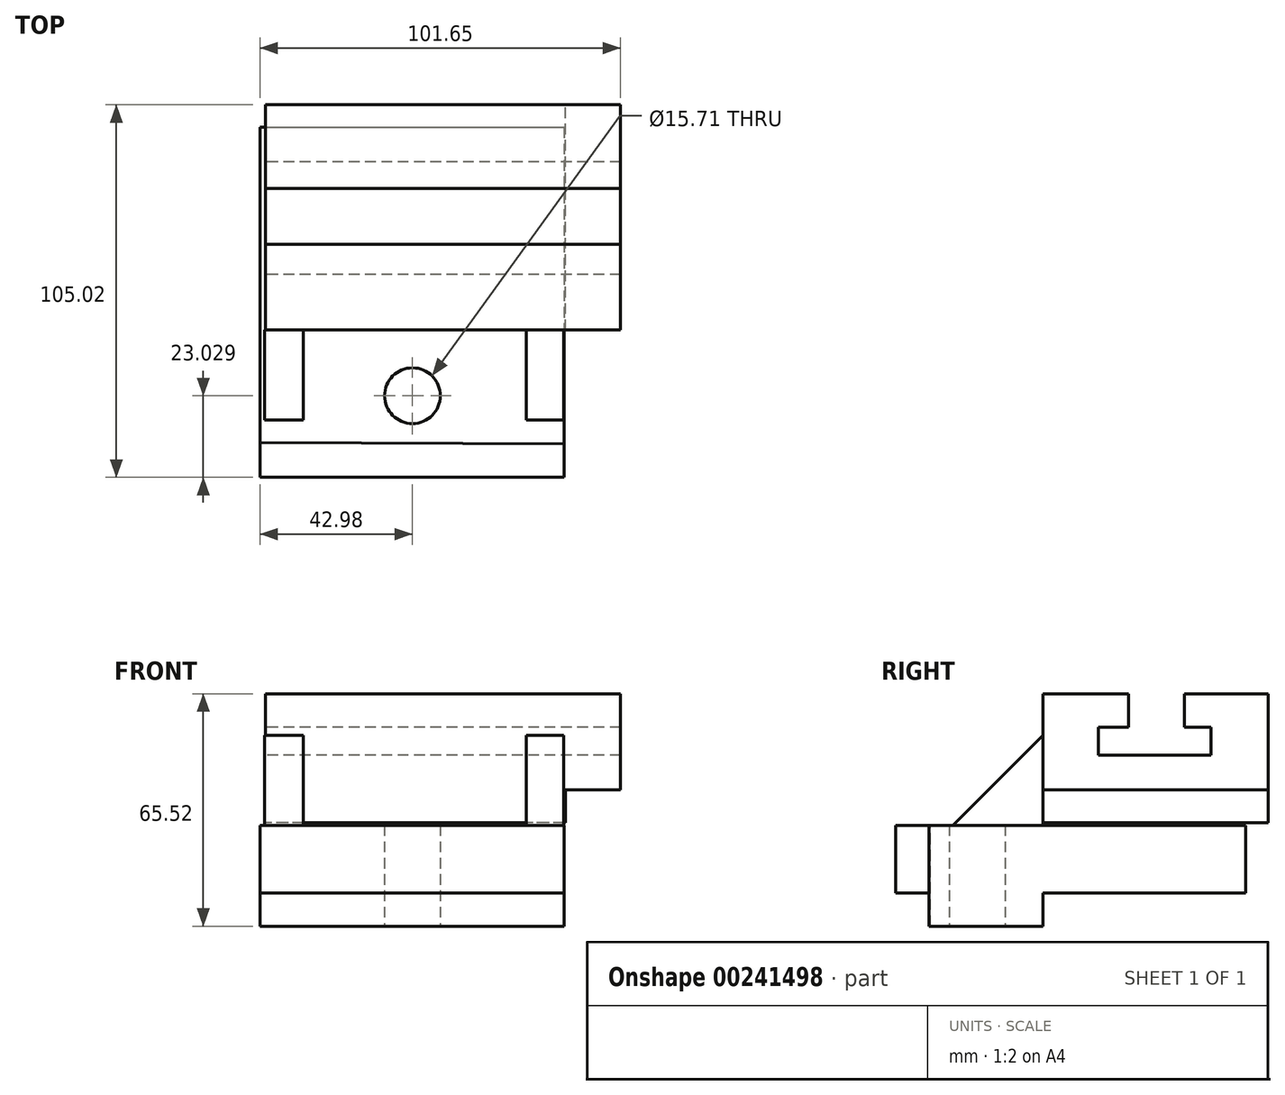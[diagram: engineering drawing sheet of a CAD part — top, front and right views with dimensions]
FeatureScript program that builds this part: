
annotation { "Feature Type Name" : "Feature", "Feature Type Description" : "" }
export const myFeature = defineFeature(function(context is Context, id is Id, definition is map)
    precondition{}
    {
        {
            var Q0;
            Q0=qCreatedBy(makeId("Top.planeOp"),FACE);
            var sketch = newSketch(context, id + "F0", { "sketchPlane" : qUnion([Q0])});
            skLineSegment(sketch, "E0", {"start": v(-42.94, 57.15) * mm, "end": v(42.75, 57.15) * mm});
            skLineSegment(sketch, "E1", {"start": v(42.75, 57.15) * mm, "end": v(42.75, -32.12) * mm});
            skLineSegment(sketch, "E2", {"start": v(42.38, -31.75) * mm, "end": v(-42.94, -31.75) * mm});
            skLineSegment(sketch, "E3", {"start": v(-42.94, -31.75) * mm, "end": v(-42.94, 57.15) * mm});
            skLineSegment(sketch, "E4", {"start": v(-42.94, 0) * mm, "end": v(42.75, 0) * mm});
            skLineSegment(sketch, "E5", {"start": v(-42.94, -31.75) * mm, "end": v(42.75, -32.12) * mm});
            skLineSegment(sketch, "E6", {"start": v(-42.94, -31.75) * mm, "end": v(-42.98, -41.52) * mm});
            skLineSegment(sketch, "E7", {"start": v(-42.98, -41.52) * mm, "end": v(42.75, -41.52) * mm});
            skLineSegment(sketch, "E8", {"start": v(42.75, -41.52) * mm, "end": v(42.75, -32.12) * mm});
            skSolve(sketch);
        }
        {
            var Q0;
            {var subQ0=sQuery(id+"F0.wireOp",EDGE,"E0");Q0=makeQuery(id+"F0.imprint","IMPRINT",FACE,{"disambiguationData":[TD([[makeQuery(id+"F0.imprint","IMPRINT",EDGE,{"derivedFrom":subQ0}),-1.0]])]});}
            extrude(context, id + "F1", {"entities" : qUnion([Q0]), "oppositeDirection" : true, "depth" : 19.05 * mm});
        }
        {
            var Q0;
            {var subQ2=sQuery(id+"F0.wireOp",EDGE,"E6");Q0=makeQuery(id+"F0.imprint","IMPRINT",FACE,{"disambiguationData":[TD([[makeQuery(id+"F0.imprint","IMPRINT",EDGE,{"derivedFrom":subQ2}),1.0]])]});}
            extrude(context, id + "F2", {"entities" : qUnion([Q0]), "oppositeDirection" : true, "depth" : 19.05 * mm});
        }
        {
            var Q0;
            {var subQ2=sQuery(id+"F0.wireOp",EDGE,"E4");Q0=makeQuery(id+"F0.imprint","IMPRINT",FACE,{"disambiguationData":[TD([[makeQuery(id+"F0.imprint","IMPRINT",EDGE,{"derivedFrom":subQ2}),-1.0]])]});}
            extrude(context, id + "F3", {"entities" : qUnion([Q0]), "oppositeDirection" : true, "depth" : 28.45 * mm});
        }
        {
            var Q0;
            Q0=qCreatedBy(makeId("Right.planeOp"),FACE);
            var sketch = newSketch(context, id + "F4", { "sketchPlane" : qUnion([Q0])});
            skLineSegment(sketch, "E9", {"start": v(0, 0) * mm, "end": v(-25.4, 0) * mm});
            skLineSegment(sketch, "E10", {"start": v(-25.4, 0) * mm, "end": v(0, 25.4) * mm});
            skLineSegment(sketch, "E11", {"start": v(0, 25.4) * mm, "end": v(0, 0) * mm});
            skSolve(sketch);
        }
        {
            var Q0;
            Q0=makeQuery(id+"F4.imprint","IMPRINT",FACE,{"disambiguationData":[TD([[makeQuery(id+"F4.imprint","IMPRINT",EDGE,{"derivedFrom":sQuery(id+"F4.wireOp",EDGE,"E9")}),-1.0]])]});
            extrude(context, id + "F5", {"entities" : qUnion([Q0]), "operationType" : NewBodyOperationType.ADD, "depth" : 42.67 * mm, "hasSecondDirection" : true, "secondDirectionOppositeDirection" : true, "secondDirectionDepth" : 41.66 * mm});
        }
        {
            var Q0;
            Q0=qCreatedBy(makeId("Front.planeOp"),FACE);
            var sketch = newSketch(context, id + "F6", { "sketchPlane" : qUnion([Q0])});
            skLineSegment(sketch, "E12", {"start": v(-30.76, 27) * mm, "end": v(-30.76, 0) * mm});
            skLineSegment(sketch, "E13", {"start": v(-30.76, 27) * mm, "end": v(32.07, 27) * mm});
            skLineSegment(sketch, "E14", {"start": v(32.07, 27) * mm, "end": v(32.07, 0) * mm});
            skLineSegment(sketch, "E15", {"start": v(32.07, 0) * mm, "end": v(-30.76, 0) * mm});
            skSolve(sketch);
        }
        {
            var Q0;
            Q0 = qSketchRegion(id + "F6", true);
            extrude(context, id + "F7", {"entities" : qUnion([Q0]), "operationType" : NewBodyOperationType.REMOVE, "depth" : 187.45 * mm});
        }
        {
            var Q0;
            Q0=qCreatedBy(makeId("Right.planeOp"),FACE);
            var sketch = newSketch(context, id + "F8", { "sketchPlane" : qUnion([Q0])});
            skLineSegment(sketch, "E16", {"start": v(0, 0.75) * mm, "end": v(63.5, 0.75) * mm});
            skLineSegment(sketch, "E17", {"start": v(0, 0.75) * mm, "end": v(0, 37.07) * mm});
            skLineSegment(sketch, "E18", {"start": v(0, 37.07) * mm, "end": v(24.14, 37.07) * mm});
            skLineSegment(sketch, "E19", {"start": v(63.5, 0.75) * mm, "end": v(63.5, 37.07) * mm});
            skLineSegment(sketch, "E20", {"start": v(63.5, 37.07) * mm, "end": v(39.89, 37.07) * mm});
            skLineSegment(sketch, "E21", {"start": v(39.89, 37.07) * mm, "end": v(39.89, 27.67) * mm});
            skLineSegment(sketch, "E22", {"start": v(39.89, 27.67) * mm, "end": v(47.45, 27.67) * mm});
            skLineSegment(sketch, "E23", {"start": v(24.14, 37.07) * mm, "end": v(24.14, 27.67) * mm});
            skLineSegment(sketch, "E24", {"start": v(24.22, 27.67) * mm, "end": v(15.7, 27.67) * mm});
            skLineSegment(sketch, "E25", {"start": v(15.7, 27.67) * mm, "end": v(15.7, 19.8) * mm});
            skLineSegment(sketch, "E26", {"start": v(15.7, 19.8) * mm, "end": v(47.46, 19.8) * mm});
            skLineSegment(sketch, "E27", {"start": v(47.46, 19.8) * mm, "end": v(47.45, 27.67) * mm});
            skSolve(sketch);
        }
        {
            var Q0;
            Q0 = qSketchRegion(id + "F8", true);
            extrude(context, id + "F9", {"entities" : qUnion([Q0]), "depth" : 58.67 * mm, "hasSecondDirection" : true, "secondDirectionOppositeDirection" : true, "secondDirectionDepth" : 41.4 * mm});
        }
        {
            var Q0;
            Q0=qCreatedBy(makeId("Front.planeOp"),FACE);
            var sketch = newSketch(context, id + "F10", { "sketchPlane" : qUnion([Q0])});
            skLineSegment(sketch, "E28", {"start": v(43.2, 9.98) * mm, "end": v(60.21, 9.98) * mm});
            skLineSegment(sketch, "E29", {"start": v(60.21, 9.98) * mm, "end": v(60.21, 0) * mm});
            skLineSegment(sketch, "E30", {"start": v(60.21, 0) * mm, "end": v(43.2, 0) * mm});
            skLineSegment(sketch, "E31", {"start": v(43.2, 0) * mm, "end": v(43.2, 9.98) * mm});
            skSolve(sketch);
        }
        {
            var Q0;
            Q0 = qSketchRegion(id + "F10", true);
            extrude(context, id + "F11", {"entities" : qUnion([Q0]), "operationType" : NewBodyOperationType.REMOVE, "oppositeDirection" : true, "depth" : 129.29 * mm});
        }
        {
            var Q0;
            Q0=qCreatedBy(makeId("Top.planeOp"),FACE);
            var sketch = newSketch(context, id + "F12", { "sketchPlane" : qUnion([Q0])});
            skCircle(sketch, "E32", {"center": v(0, -18.5) * mm, "radius": 7.85 * mm});
            skSolve(sketch);
        }
        {
            var Q0;
            Q0 = qSketchRegion(id + "F12", true);
            extrude(context, id + "F13", {"entities" : qUnion([Q0]), "operationType" : NewBodyOperationType.REMOVE, "depth" : 60.7 * mm, "hasSecondDirection" : true, "secondDirectionOppositeDirection" : true, "secondDirectionDepth" : 80.52 * mm});
        }
    });
